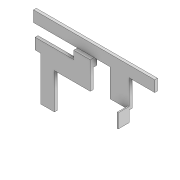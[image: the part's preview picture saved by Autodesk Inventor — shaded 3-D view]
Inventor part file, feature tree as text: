
AUTODESK INVENTOR PART (.ipt)
format: ipt  version: 2021 (Build 250183000, 183)  size: 332,800 bytes
history: native  units: in
note: dims shown in document units (in); Inventor stores cm internally (conversion verified against a paired STEP export)
features: extrude x26, sketch x26, projected_geometry x22
ambient origin geometry x8: Origin, YZ Plane, XZ Plane, XY Plane, X Axis, Y Axis, Z Axis, Center Point
bodies: Solid1 (feature_tree)
feature tree (74):
  extrude  "Extrusion1"  Depth=0.0787in
  extrude  "Extrusion2"  Depth=0.2756in
  extrude  "Extrusion3"  Depth=0.1181in
  extrude  "Extrusion4"  Depth=0.0787in
  extrude  "Extrusion5"  Depth=0.0787in
  extrude  "Extrusion6"  Depth=0.0787in
  extrude  "Extrusion7"  Depth=0.0197in
  extrude  "Extrusion8"  Depth=0.0787in TaperAngle=0.0deg
  extrude  "Extrusion9"  Depth=0.0276in TaperAngle=0.0deg
  extrude  "Extrusion10"  Depth=0.0591in TaperAngle=0.0deg
  extrude  "Extrusion11"  Depth=0.0197in TaperAngle=0.0deg
  extrude  "Extrusion12"  Depth=0.0079in TaperAngle=0.0deg
  extrude  "Extrusion13"  Depth=0.0197in TaperAngle=0.0deg
  extrude  "Extrusion14"  Depth=0.0197in TaperAngle=0.0deg
  extrude  "Extrusion15"  Depth=0.0016in TaperAngle=0.0deg
  extrude  "Extrusion16"  Depth=0.0049in TaperAngle=0.0deg
  extrude  "Extrusion17"  Depth=0.0787in TaperAngle=0.0deg
  extrude  "Extrusion18"  Depth=0.0591in TaperAngle=0.0deg
  extrude  "Extrusion19"  Depth=0.0787in TaperAngle=0.0deg
  extrude  "Extrusion20"  Depth=0.0197in TaperAngle=0.0deg
  extrude  "Extrusion21"  [1 undecoded]
  extrude  "Extrusion22"  [1 undecoded]
  extrude  "Extrusion23"  [1 undecoded]
  extrude  "Extrusion24"  [1 undecoded]
  extrude  "Extrusion25"  [1 undecoded]
  extrude  "Extrusion26"  [1 undecoded]
  sketch  "Sketch1"  dims[d0=0.8661in d1=0.0787in]
  sketch  "Sketch2"  dims[d2=0.2283in d3=0.2756in]
  sketch  "Sketch3"  dims[d4=0.1181in d5=0.0866in]
  projected_geometry  "Projected Loop1"
  sketch  "Sketch4"  dims[d8=0.2756in d9=0.0787in]
  projected_geometry  "Projected Loop2"
  sketch  "Sketch5"  dims[d11=0.315in d12=0.0787in]
  projected_geometry  "Projected Loop3"
  sketch  "Sketch6"  dims[d13=0.0197in d14=0.0787in]
  sketch  "Sketch7"  dims[d15=0.0197in d16=0.0in d17=0.0197in]
  projected_geometry  "Projected Loop4"
  sketch  "Sketch8"  dims[d18=0.0787in d19=0.0787in d20=0.0in]
  projected_geometry  "Projected Loop5"
  sketch  "Sketch9"  dims[d21=0.0197in d22=0.0in d23=0.0276in d24=0.0in]
  projected_geometry  "Projected Loop6"
  sketch  "Sketch10"  dims[d25=0.0197in d26=0.0in d27=0.0591in d28=0.0in]
  projected_geometry  "Projected Loop7"
  sketch  "Sketch11"  dims[d29=0.0197in d30=0.0in d31=0.0197in d32=0.0in]
  projected_geometry  "Projected Loop8"
  sketch  "Sketch12"  dims[d33=0.0079in d34=0.0in d35=0.0118in d36=0.0in]
  projected_geometry  "Projected Loop9"
  sketch  "Sketch13"  dims[d37=0.0118in d38=0.0in d39=0.0197in d40=0.0in]
  projected_geometry  "Projected Loop10"
  sketch  "Sketch14"  dims[d41=0.0197in d42=0.0in d43=0.0118in d44=0.0in]
  projected_geometry  "Projected Loop11"
  sketch  "Sketch15"  dims[d45=0.0118in d46=0.0in d47=0.0016in d48=0.0in]
  projected_geometry  "Projected Loop12"
  sketch  "Sketch16"  dims[d49=0.0049in d50=0.0in d51=0.0049in d52=0.0in]
  projected_geometry  "Projected Loop13"
  sketch  "Sketch17"  dims[d53=0.0463in d54=0.0in d55=0.0787in d56=0.0in]
  projected_geometry  "Projected Loop14"
  sketch  "Sketch18"  dims[d57=0.0772in d58=0.0in d59=0.0591in d60=0.0in]
  projected_geometry  "Projected Loop15"
  sketch  "Sketch19"  dims[d61=0.0787in d62=0.0in d63=0.0295in d64=0.0in]
  projected_geometry  "Projected Loop16"
  sketch  "Sketch20"  dims[d65=0.0118in d66=0.0in d67=0.0197in d68=0.0in]
  projected_geometry  "Projected Loop17"
  sketch  "Sketch21"
  projected_geometry  "Projected Loop18"
  sketch  "Sketch22"
  projected_geometry  "Projected Loop19"
  sketch  "Sketch23"
  sketch  "Sketch24"
  projected_geometry  "Projected Loop20"
  sketch  "Sketch25"
  projected_geometry  "Projected Loop21"
  sketch  "Sketch26"
  projected_geometry  "Projected Loop22"
note: 6 required parameter values undecoded (feature->parameter linkage not recoverable at this tier; creation-order binding heuristic only, values carry confidence <= 0.55)
